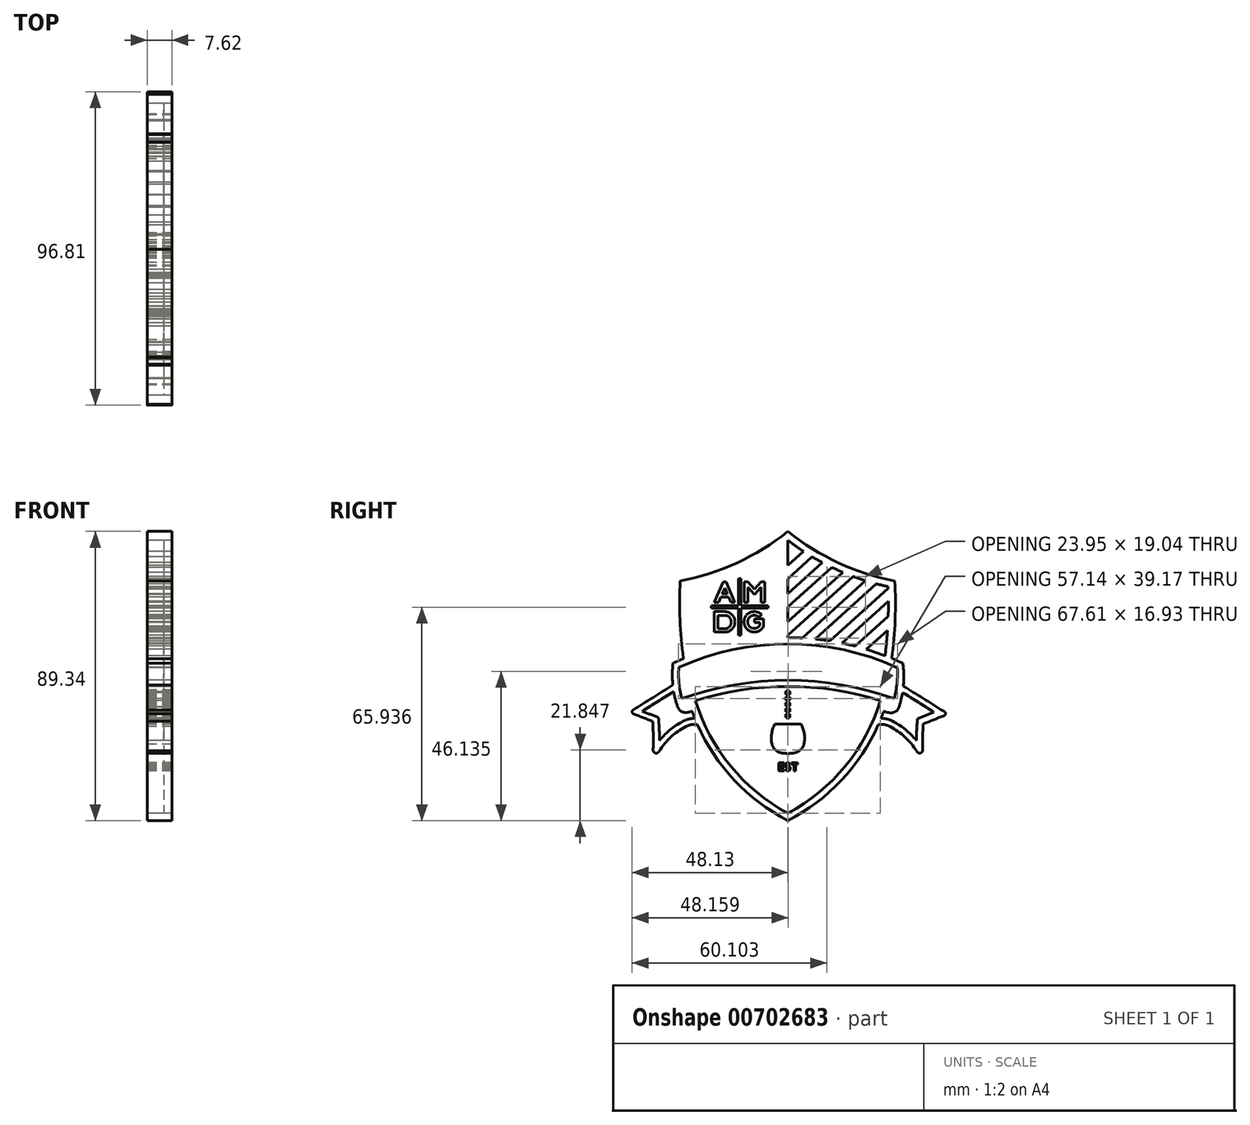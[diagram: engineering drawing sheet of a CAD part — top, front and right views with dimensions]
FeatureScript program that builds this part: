
annotation { "Feature Type Name" : "Feature", "Feature Type Description" : "" }
export const myFeature = defineFeature(function(context is Context, id is Id, definition is map)
    precondition{}
    {
        {
            var Q0;
            Q0=qCreatedBy(makeId("Right.planeOp"),FACE);
            var sketch = newSketch(context, id + "F0", { "sketchPlane" : qUnion([Q0])});
            skArc(sketch, "E0", {"start": v(-30.47, -7.29) * mm, "mid": v(-18.91, -28.58) * mm, "end": v(0, -43.73) * mm});
            skLineSegment(sketch, "E1", {"start": v(0, -43.73) * mm, "end": v(0, -41.47) * mm});
            skArc(sketch, "E2", {"start": v(0, -41.47) * mm, "mid": v(17.72, -26.9) * mm, "end": v(28.57, -6.67) * mm});
            skArc(sketch, "E3", {"start": v(0, -43.73) * mm, "mid": v(18.91, -28.58) * mm, "end": v(30.47, -7.29) * mm});
            skArc(sketch, "E4", {"start": v(-28.57, -6.67) * mm, "mid": v(-17.72, -26.9) * mm, "end": v(0, -41.47) * mm});
            skLineSegment(sketch, "E5", {"start": v(-14.58, 21.87) * mm, "end": v(-6.19, 21.87) * mm});
            skLineSegment(sketch, "E6", {"start": v(-6.19, 21.87) * mm, "end": v(-6.19, 22.63) * mm});
            skLineSegment(sketch, "E7", {"start": v(-6.19, 22.63) * mm, "end": v(-14.58, 22.63) * mm});
            skLineSegment(sketch, "E8", {"start": v(-14.58, 22.63) * mm, "end": v(-14.58, 31.02) * mm});
            skLineSegment(sketch, "E9", {"start": v(-14.58, 31.02) * mm, "end": v(-15.34, 31.02) * mm});
            skLineSegment(sketch, "E10", {"start": v(-15.34, 22.63) * mm, "end": v(-23.73, 22.63) * mm});
            skLineSegment(sketch, "E11", {"start": v(-23.73, 22.63) * mm, "end": v(-23.73, 21.87) * mm});
            skLineSegment(sketch, "E12", {"start": v(-15.34, 21.87) * mm, "end": v(-15.34, 13.48) * mm});
            skLineSegment(sketch, "E13", {"start": v(-15.34, 13.48) * mm, "end": v(-14.58, 13.48) * mm});
            skLineSegment(sketch, "E14", {"start": v(-14.58, 13.48) * mm, "end": v(-14.58, 21.87) * mm});
            skLineSegment(sketch, "E15", {"start": v(-19.04, 30) * mm, "end": v(-20.03, 30) * mm});
            skLineSegment(sketch, "E16", {"start": v(-20.03, 30) * mm, "end": v(-22.71, 23.64) * mm});
            skLineSegment(sketch, "E17", {"start": v(-15.34, 31.02) * mm, "end": v(-15.34, 22.63) * mm});
            skLineSegment(sketch, "E18", {"start": v(-16.35, 23.64) * mm, "end": v(-17.62, 23.64) * mm});
            skLineSegment(sketch, "E19", {"start": v(-22.71, 23.64) * mm, "end": v(-21.43, 23.64) * mm});
            skLineSegment(sketch, "E20", {"start": v(-20.3, 26.31) * mm, "end": v(-18.75, 26.31) * mm});
            skLineSegment(sketch, "E21", {"start": v(-18.75, 26.31) * mm, "end": v(-19.53, 28.16) * mm});
            skLineSegment(sketch, "E22", {"start": v(-20.3, 26.31) * mm, "end": v(-19.53, 28.16) * mm});
            skLineSegment(sketch, "E23", {"start": v(-20.74, 25.3) * mm, "end": v(-21.43, 23.64) * mm});
            skLineSegment(sketch, "E24", {"start": v(-20.74, 25.3) * mm, "end": v(-18.32, 25.3) * mm});
            skLineSegment(sketch, "E25", {"start": v(-18.32, 25.3) * mm, "end": v(-17.62, 23.64) * mm});
            skLineSegment(sketch, "E26", {"start": v(-12.42, 23.64) * mm, "end": v(-12.42, 28.45) * mm});
            skLineSegment(sketch, "E27", {"start": v(-7.2, 23.64) * mm, "end": v(-8.36, 23.64) * mm});
            skLineSegment(sketch, "E28", {"start": v(-8.36, 23.64) * mm, "end": v(-8.36, 28.45) * mm});
            skLineSegment(sketch, "E29", {"start": v(-12.42, 28.45) * mm, "end": v(-10.39, 26.16) * mm});
            skLineSegment(sketch, "E30", {"start": v(-10.39, 26.16) * mm, "end": v(-8.36, 28.45) * mm});
            skLineSegment(sketch, "E31", {"start": v(-7.2, 30) * mm, "end": v(-7.2, 23.64) * mm});
            skLineSegment(sketch, "E32", {"start": v(-12.42, 23.64) * mm, "end": v(-13.56, 23.64) * mm});
            skLineSegment(sketch, "E33", {"start": v(-13.56, 30) * mm, "end": v(-13.56, 23.64) * mm});
            skLineSegment(sketch, "E34", {"start": v(-19.04, 30) * mm, "end": v(-16.35, 23.64) * mm});
            skLineSegment(sketch, "E35", {"start": v(-7.2, 30) * mm, "end": v(-8.36, 30) * mm});
            skLineSegment(sketch, "E36", {"start": v(-8.36, 30) * mm, "end": v(-10.39, 27.79) * mm});
            skLineSegment(sketch, "E37", {"start": v(-13.56, 30) * mm, "end": v(-12.42, 30) * mm});
            skLineSegment(sketch, "E38", {"start": v(-12.42, 30) * mm, "end": v(-10.39, 27.79) * mm});
            skLineSegment(sketch, "E39", {"start": v(-22.71, 20.84) * mm, "end": v(-22.71, 14.5) * mm});
            skLineSegment(sketch, "E40", {"start": v(-21.58, 15.52) * mm, "end": v(-21.58, 19.69) * mm});
            skLineSegment(sketch, "E41", {"start": v(-23.73, 21.87) * mm, "end": v(-15.34, 21.87) * mm});
            skLineSegment(sketch, "E42", {"start": v(-8.96, 19.12) * mm, "end": v(-8.15, 19.93) * mm});
            skLineSegment(sketch, "E43", {"start": v(-10.3, 18.56) * mm, "end": v(-7.6, 18.56) * mm});
            skLineSegment(sketch, "E44", {"start": v(-10.3, 18.56) * mm, "end": v(-10.3, 17.42) * mm});
            skLineSegment(sketch, "E45", {"start": v(-10.3, 17.42) * mm, "end": v(-8.73, 17.42) * mm});
            skArc(sketch, "E46", {"start": v(34.3, -8.67) * mm, "mid": v(0.13, -2.3) * mm, "end": v(-34.07, -8.58) * mm});
            skArc(sketch, "E47", {"start": v(34.3, -8.67) * mm, "mid": v(35.68, -1.97) * mm, "end": v(35.5, 4.87) * mm});
            skArc(sketch, "E48", {"start": v(-35.5, 4.87) * mm, "mid": v(-35.55, -1.94) * mm, "end": v(-34.07, -8.58) * mm});
            skArc(sketch, "E49", {"start": v(31.82, -12.76) * mm, "mid": v(30.32, -12.3) * mm, "end": v(28.76, -12.14) * mm});
            skArc(sketch, "E50", {"start": v(39.69, -19) * mm, "mid": v(36.1, -15.44) * mm, "end": v(31.82, -12.76) * mm});
            skArc(sketch, "E51", {"start": v(40.04, -12.2) * mm, "mid": v(39.79, -15.6) * mm, "end": v(39.69, -19) * mm});
            skArc(sketch, "E52", {"start": v(40.04, -12.2) * mm, "mid": v(42.57, -11.26) * mm, "end": v(45.08, -10.26) * mm});
            skArc(sketch, "E53", {"start": v(45.08, -10.26) * mm, "mid": v(40.29, -7.15) * mm, "end": v(35.4, -4.2) * mm});
            skArc(sketch, "E54", {"start": v(41.83, -13.82) * mm, "mid": v(41.63, -17.96) * mm, "end": v(41.66, -22.11) * mm});
            skArc(sketch, "E55", {"start": v(47.88, -11.44) * mm, "mid": v(48.68, -10.69) * mm, "end": v(47.93, -9.9) * mm});
            skArc(sketch, "E56", {"start": v(41.83, -13.82) * mm, "mid": v(44.86, -12.64) * mm, "end": v(47.88, -11.44) * mm});
            skArc(sketch, "E57", {"start": v(47.93, -9.9) * mm, "mid": v(41.81, -6) * mm, "end": v(35.66, -2.16) * mm});
            skArc(sketch, "E58", {"start": v(31.55, -14.68) * mm, "mid": v(29.8, -14.07) * mm, "end": v(27.95, -14.05) * mm});
            skArc(sketch, "E59", {"start": v(39.78, -22.32) * mm, "mid": v(40.8, -22.88) * mm, "end": v(41.66, -22.11) * mm});
            skArc(sketch, "E60", {"start": v(39.78, -22.32) * mm, "mid": v(36.2, -17.94) * mm, "end": v(31.55, -14.68) * mm});
            skArc(sketch, "E61", {"start": v(-40, -11.94) * mm, "mid": v(-42.5, -10.91) * mm, "end": v(-45.03, -9.99) * mm});
            skArc(sketch, "E62", {"start": v(-31.82, -12.76) * mm, "mid": v(-36.1, -15.44) * mm, "end": v(-39.69, -19) * mm});
            skArc(sketch, "E63", {"start": v(-39.69, -19) * mm, "mid": v(-39.76, -15.47) * mm, "end": v(-40, -11.94) * mm});
            skArc(sketch, "E64", {"start": v(-35.27, -3.92) * mm, "mid": v(-40.2, -6.87) * mm, "end": v(-45.03, -9.99) * mm});
            skArc(sketch, "E65", {"start": v(-28.76, -12.14) * mm, "mid": v(-30.32, -12.3) * mm, "end": v(-31.82, -12.76) * mm});
            skArc(sketch, "E66", {"start": v(-35.55, -1.89) * mm, "mid": v(-41.74, -5.73) * mm, "end": v(-47.89, -9.62) * mm});
            skArc(sketch, "E67", {"start": v(-47.85, -10.66) * mm, "mid": v(-44.83, -11.86) * mm, "end": v(-41.8, -13.04) * mm});
            skArc(sketch, "E68", {"start": v(-41.66, -22.11) * mm, "mid": v(-41.59, -17.57) * mm, "end": v(-41.8, -13.04) * mm});
            skArc(sketch, "E69", {"start": v(-31.55, -14.68) * mm, "mid": v(-36.2, -17.94) * mm, "end": v(-39.78, -22.32) * mm});
            skArc(sketch, "E70", {"start": v(-41.66, -22.11) * mm, "mid": v(-40.8, -22.88) * mm, "end": v(-39.78, -22.32) * mm});
            skArc(sketch, "E71", {"start": v(-27.95, -14.05) * mm, "mid": v(-29.8, -14.07) * mm, "end": v(-31.55, -14.68) * mm});
            skArc(sketch, "E72", {"start": v(-47.89, -9.62) * mm, "mid": v(-48.13, -10.15) * mm, "end": v(-47.85, -10.66) * mm});
            skArc(sketch, "E73", {"start": v(-33.7, 3.57) * mm, "mid": v(-33.65, -1.27) * mm, "end": v(-32.82, -6.05) * mm});
            skArc(sketch, "E74", {"start": v(32.85, -6.06) * mm, "mid": v(33.69, -1.3) * mm, "end": v(33.8, 3.53) * mm});
            skArc(sketch, "E75", {"start": v(31.94, -10.43) * mm, "mid": v(33.41, -9.94) * mm, "end": v(34.3, -8.67) * mm});
            skArc(sketch, "E76", {"start": v(-34.07, -8.58) * mm, "mid": v(-33.17, -9.85) * mm, "end": v(-31.7, -10.34) * mm});
            skArc(sketch, "E77", {"start": v(29.6, -9.9) * mm, "mid": v(30.74, -10.3) * mm, "end": v(31.94, -10.43) * mm});
            skArc(sketch, "E78", {"start": v(-31.7, -10.34) * mm, "mid": v(-30.63, -10.23) * mm, "end": v(-29.6, -9.9) * mm});
            skLineSegment(sketch, "E79", {"start": v(-7.6, 18.56) * mm, "end": v(-7.6, 16.28) * mm});
            skLineSegment(sketch, "E80", {"start": v(-8.73, 17.42) * mm, "end": v(-8.73, 16.6) * mm});
            skArc(sketch, "E81", {"start": v(-7.64, 16.08) * mm, "mid": v(-7.6, 16.18) * mm, "end": v(-7.6, 16.28) * mm});
            skArc(sketch, "E82", {"start": v(-8.82, 16.38) * mm, "mid": v(-8.75, 16.48) * mm, "end": v(-8.73, 16.6) * mm});
            skArc(sketch, "E83", {"start": v(-8.96, 19.12) * mm, "mid": v(-12.43, 17.57) * mm, "end": v(-8.82, 16.38) * mm});
            skArc(sketch, "E84", {"start": v(-8.15, 19.93) * mm, "mid": v(-13.54, 17.26) * mm, "end": v(-7.64, 16.08) * mm});
            skLineSegment(sketch, "E85", {"start": v(-22.71, 20.84) * mm, "end": v(-19.55, 20.84) * mm});
            skLineSegment(sketch, "E86", {"start": v(-22.71, 14.5) * mm, "end": v(-19.55, 14.5) * mm});
            skArc(sketch, "E87", {"start": v(-19.55, 14.5) * mm, "mid": v(-16.35, 17.67) * mm, "end": v(-19.55, 20.84) * mm});
            skLineSegment(sketch, "E88", {"start": v(-21.58, 15.52) * mm, "end": v(-19.55, 15.52) * mm});
            skLineSegment(sketch, "E89", {"start": v(-21.58, 19.69) * mm, "end": v(-19.55, 19.69) * mm});
            skArc(sketch, "E90", {"start": v(-19.55, 15.52) * mm, "mid": v(-17.5, 17.6) * mm, "end": v(-19.55, 19.69) * mm});
            skArc(sketch, "E91", {"start": v(35.5, 4.87) * mm, "mid": v(0, 12.8) * mm, "end": v(-35.5, 4.87) * mm});
            skLineSegment(sketch, "E92", {"start": v(0, 12.8) * mm, "end": v(0, 10.87) * mm});
            skArc(sketch, "E93", {"start": v(32.09, 6.38) * mm, "mid": v(33.12, 18.33) * mm, "end": v(33.02, 30.33) * mm});
            skArc(sketch, "E94", {"start": v(30, 7.22) * mm, "mid": v(30.93, 17.87) * mm, "end": v(30.93, 28.56) * mm});
            skLineSegment(sketch, "E95", {"start": v(0, 42.88) * mm, "end": v(0, 12.8) * mm});
            skArc(sketch, "E96", {"start": v(-30.92, 28.57) * mm, "mid": v(-30.9, 18) * mm, "end": v(-29.98, 7.47) * mm});
            skArc(sketch, "E97", {"start": v(-33.27, 30.28) * mm, "mid": v(-33.34, 18.27) * mm, "end": v(-32.27, 6.3) * mm});
            skArc(sketch, "E98", {"start": v(-30.92, 28.57) * mm, "mid": v(-14.68, 34.03) * mm, "end": v(0, 42.88) * mm});
            skArc(sketch, "E99", {"start": v(0, 42.88) * mm, "mid": v(14.66, 34) * mm, "end": v(30.93, 28.56) * mm});
            skArc(sketch, "E100", {"start": v(0, 45.61) * mm, "mid": v(15.57, 35.94) * mm, "end": v(33.02, 30.33) * mm});
            skArc(sketch, "E101", {"start": v(-33.27, 30.28) * mm, "mid": v(-15.7, 35.93) * mm, "end": v(0, 45.61) * mm});
            skLineSegment(sketch, "E102", {"start": v(4.8, 39.47) * mm, "end": v(0, 35.12) * mm});
            skLineSegment(sketch, "E103", {"start": v(7.5, 37.77) * mm, "end": v(0, 30.99) * mm});
            skLineSegment(sketch, "E104", {"start": v(10.62, 36.01) * mm, "end": v(0, 26.4) * mm});
            skLineSegment(sketch, "E105", {"start": v(13.55, 34.52) * mm, "end": v(0, 22.27) * mm});
            skLineSegment(sketch, "E106", {"start": v(16.92, 33) * mm, "end": v(0, 17.69) * mm});
            skLineSegment(sketch, "E107", {"start": v(20.1, 31.73) * mm, "end": v(0, 13.55) * mm});
            skLineSegment(sketch, "E108", {"start": v(23.95, 30.4) * mm, "end": v(4.36, 12.69) * mm});
            skLineSegment(sketch, "E109", {"start": v(27.27, 29.44) * mm, "end": v(8.4, 12.38) * mm});
            skLineSegment(sketch, "E110", {"start": v(12.97, 11.79) * mm, "end": v(30.95, 28.05) * mm});
            skLineSegment(sketch, "E111", {"start": v(31.04, 24.03) * mm, "end": v(16.75, 11.1) * mm});
            skLineSegment(sketch, "E112", {"start": v(30.98, 19.34) * mm, "end": v(20.77, 10.17) * mm});
            skLineSegment(sketch, "E113", {"start": v(24.27, 9.2) * mm, "end": v(30.77, 15.07) * mm});
            skArc(sketch, "E114", {"start": v(33.8, 3.53) * mm, "mid": v(0.05, 10.87) * mm, "end": v(-33.7, 3.57) * mm});
            skArc(sketch, "E115", {"start": v(32.85, -6.06) * mm, "mid": v(0.02, -0.36) * mm, "end": v(-32.82, -6.05) * mm});
            skSolve(sketch);
        }
        {
            var Q0;
            Q0=qCreatedBy(makeId("Right.planeOp"),FACE);
            var sketch = newSketch(context, id + "F1", { "sketchPlane" : qUnion([Q0])});
            skLineSegment(sketch, "E116", {"start": v(0, -3.35) * mm, "end": v(0.9, -4.25) * mm});
            skLineSegment(sketch, "E117", {"start": v(-0.9, -4.25) * mm, "end": v(0, -3.35) * mm});
            skLineSegment(sketch, "E118", {"start": v(-0.9, -4.25) * mm, "end": v(0, -5.14) * mm});
            skLineSegment(sketch, "E119", {"start": v(0, -5.14) * mm, "end": v(0.9, -4.25) * mm});
            skLineSegment(sketch, "E120", {"start": v(0, -5.14) * mm, "end": v(-0.9, -6.03) * mm});
            skLineSegment(sketch, "E121", {"start": v(-0.9, -6.03) * mm, "end": v(0, -6.92) * mm});
            skLineSegment(sketch, "E122", {"start": v(0, -5.14) * mm, "end": v(0.9, -6.03) * mm});
            skLineSegment(sketch, "E123", {"start": v(0.9, -6.03) * mm, "end": v(0, -6.92) * mm});
            skLineSegment(sketch, "E124", {"start": v(0, -6.92) * mm, "end": v(-0.9, -7.82) * mm});
            skLineSegment(sketch, "E125", {"start": v(0, -6.92) * mm, "end": v(0.9, -7.82) * mm});
            skLineSegment(sketch, "E126", {"start": v(0.9, -7.82) * mm, "end": v(0, -8.71) * mm});
            skLineSegment(sketch, "E127", {"start": v(0, -8.71) * mm, "end": v(-0.9, -7.82) * mm});
            skLineSegment(sketch, "E128", {"start": v(0, -8.71) * mm, "end": v(0.9, -9.6) * mm});
            skLineSegment(sketch, "E129", {"start": v(0, -8.71) * mm, "end": v(-0.9, -9.6) * mm});
            skLineSegment(sketch, "E130", {"start": v(-0.9, -9.6) * mm, "end": v(0, -10.5) * mm});
            skLineSegment(sketch, "E131", {"start": v(0.9, -9.6) * mm, "end": v(0, -10.5) * mm});
            skLineSegment(sketch, "E132", {"start": v(0.9, -11.39) * mm, "end": v(0, -10.5) * mm});
            skLineSegment(sketch, "E133", {"start": v(-0.9, -11.39) * mm, "end": v(0, -12.28) * mm});
            skLineSegment(sketch, "E134", {"start": v(0.9, -11.39) * mm, "end": v(0, -12.28) * mm});
            skLineSegment(sketch, "E135", {"start": v(-0.9, -11.39) * mm, "end": v(0, -10.5) * mm});
            skLineSegment(sketch, "E136", {"start": v(0, -10.96) * mm, "end": v(-0.45, -11.4) * mm});
            skLineSegment(sketch, "E137", {"start": v(0, -10.96) * mm, "end": v(0.45, -11.4) * mm});
            skLineSegment(sketch, "E138", {"start": v(0.45, -11.4) * mm, "end": v(0, -11.86) * mm});
            skLineSegment(sketch, "E139", {"start": v(0, -11.86) * mm, "end": v(-0.45, -11.4) * mm});
            skLineSegment(sketch, "E140", {"start": v(0, -10.07) * mm, "end": v(0.45, -9.62) * mm});
            skLineSegment(sketch, "E141", {"start": v(0.45, -9.62) * mm, "end": v(0, -9.17) * mm});
            skLineSegment(sketch, "E142", {"start": v(0, -9.17) * mm, "end": v(-0.45, -9.62) * mm});
            skLineSegment(sketch, "E143", {"start": v(-0.45, -9.62) * mm, "end": v(0, -10.07) * mm});
            skLineSegment(sketch, "E144", {"start": v(0, -7.38) * mm, "end": v(-0.45, -7.83) * mm});
            skLineSegment(sketch, "E145", {"start": v(-0.45, -7.83) * mm, "end": v(0, -8.28) * mm});
            skLineSegment(sketch, "E146", {"start": v(0, -8.28) * mm, "end": v(0.45, -7.83) * mm});
            skLineSegment(sketch, "E147", {"start": v(0.45, -7.83) * mm, "end": v(0, -7.38) * mm});
            skLineSegment(sketch, "E148", {"start": v(0, -6.49) * mm, "end": v(0.45, -6.04) * mm});
            skLineSegment(sketch, "E149", {"start": v(0.45, -6.04) * mm, "end": v(0, -5.6) * mm});
            skLineSegment(sketch, "E150", {"start": v(0, -5.6) * mm, "end": v(-0.45, -6.04) * mm});
            skLineSegment(sketch, "E151", {"start": v(-0.45, -6.04) * mm, "end": v(0, -6.49) * mm});
            skLineSegment(sketch, "E152", {"start": v(0, -3.8) * mm, "end": v(0.45, -4.24) * mm});
            skLineSegment(sketch, "E153", {"start": v(0.45, -4.24) * mm, "end": v(0, -4.69) * mm});
            skLineSegment(sketch, "E154", {"start": v(-0.45, -4.24) * mm, "end": v(0, -4.69) * mm});
            skLineSegment(sketch, "E155", {"start": v(-0.45, -4.24) * mm, "end": v(0, -3.8) * mm});
            skLineSegment(sketch, "E156", {"start": v(0, -30) * mm, "end": v(0, -34.18) * mm});
            skLineSegment(sketch, "E157", {"start": v(0, -34.18) * mm, "end": v(5.89, -34.18) * mm});
            skLineSegment(sketch, "E158", {"start": v(5.89, -34.18) * mm, "end": v(5.89, -30) * mm});
            skLineSegment(sketch, "E159", {"start": v(5.89, -30) * mm, "end": v(0, -30) * mm});
            skLineSegment(sketch, "E160", {"start": v(0, -30) * mm, "end": v(-5.89, -30) * mm});
            skLineSegment(sketch, "E161", {"start": v(-5.89, -30) * mm, "end": v(-5.89, -34.18) * mm});
            skLineSegment(sketch, "E162", {"start": v(-5.89, -34.18) * mm, "end": v(0, -34.18) * mm});
            skLineSegment(sketch, "E163", {"start": v(-0.25, -27.7) * mm, "end": v(-0.73, -27.88) * mm});
            skLineSegment(sketch, "E164", {"start": v(0.23, -26.47) * mm, "end": v(0.7, -26.28) * mm});
            skLineSegment(sketch, "E165", {"start": v(1.13, -26.3) * mm, "end": v(1.13, -25.8) * mm});
            skLineSegment(sketch, "E166", {"start": v(1.13, -25.8) * mm, "end": v(3.03, -25.8) * mm});
            skLineSegment(sketch, "E167", {"start": v(3.03, -25.8) * mm, "end": v(3.03, -26.3) * mm});
            skLineSegment(sketch, "E168", {"start": v(2.33, -26.3) * mm, "end": v(3.03, -26.3) * mm});
            skLineSegment(sketch, "E169", {"start": v(1.83, -26.3) * mm, "end": v(1.13, -26.3) * mm});
            skLineSegment(sketch, "E170", {"start": v(1.83, -26.3) * mm, "end": v(1.83, -28.34) * mm});
            skLineSegment(sketch, "E171", {"start": v(1.83, -28.34) * mm, "end": v(2.33, -28.34) * mm});
            skLineSegment(sketch, "E172", {"start": v(2.33, -28.34) * mm, "end": v(2.33, -26.3) * mm});
            skLineSegment(sketch, "E173", {"start": v(-1.14, -26.3) * mm, "end": v(-1.14, -25.8) * mm});
            skLineSegment(sketch, "E174", {"start": v(-1.14, -28.34) * mm, "end": v(-1.14, -27.83) * mm});
            skLineSegment(sketch, "E175", {"start": v(-2.3, -26.3) * mm, "end": v(-2.3, -26.8) * mm});
            skLineSegment(sketch, "E176", {"start": v(-2.3, -27.31) * mm, "end": v(-2.3, -27.83) * mm});
            skLineSegment(sketch, "E177", {"start": v(-2.8, -25.8) * mm, "end": v(-2.8, -28.34) * mm});
            skLineSegment(sketch, "E178", {"start": v(-2.8, -25.8) * mm, "end": v(-1.14, -25.8) * mm});
            skLineSegment(sketch, "E179", {"start": v(-1.14, -28.34) * mm, "end": v(-2.8, -28.34) * mm});
            skLineSegment(sketch, "E180", {"start": v(-2.3, -26.3) * mm, "end": v(-1.14, -26.3) * mm});
            skLineSegment(sketch, "E181", {"start": v(-2.3, -27.83) * mm, "end": v(-1.14, -27.83) * mm});
            skLineSegment(sketch, "E182", {"start": v(-1.27, -26.8) * mm, "end": v(-1.27, -27.31) * mm});
            skLineSegment(sketch, "E183", {"start": v(-1.27, -27.31) * mm, "end": v(-2.3, -27.31) * mm});
            skLineSegment(sketch, "E184", {"start": v(-2.3, -26.8) * mm, "end": v(-1.27, -26.8) * mm});
            skLineSegment(sketch, "E185", {"start": v(0, -13.91) * mm, "end": v(4.06, -13.91) * mm});
            skLineSegment(sketch, "E186", {"start": v(0, -13.91) * mm, "end": v(-4.06, -13.91) * mm});
            skArc(sketch, "E187", {"start": v(4.95, -20.14) * mm, "mid": v(5.06, -16.95) * mm, "end": v(4.06, -13.91) * mm});
            skArc(sketch, "E188", {"start": v(1.92, -22.83) * mm, "mid": v(3.82, -21.91) * mm, "end": v(4.95, -20.14) * mm});
            skArc(sketch, "E189", {"start": v(-4.93, -20.14) * mm, "mid": v(-3.8, -21.91) * mm, "end": v(-1.9, -22.83) * mm});
            skArc(sketch, "E190", {"start": v(-4.06, -13.91) * mm, "mid": v(-5.04, -16.95) * mm, "end": v(-4.93, -20.14) * mm});
            skArc(sketch, "E191", {"start": v(-1.9, -22.83) * mm, "mid": v(0, -23) * mm, "end": v(1.92, -22.83) * mm});
            skArc(sketch, "E192", {"start": v(-0.73, -27.88) * mm, "mid": v(0.63, -28.03) * mm, "end": v(0, -26.83) * mm});
            skArc(sketch, "E193", {"start": v(-0.25, -27.7) * mm, "mid": v(0.2, -27.74) * mm, "end": v(0, -27.34) * mm});
            skArc(sketch, "E194", {"start": v(0.7, -26.28) * mm, "mid": v(-0.65, -26.14) * mm, "end": v(0, -27.34) * mm});
            skArc(sketch, "E195", {"start": v(0.23, -26.47) * mm, "mid": v(-0.22, -26.43) * mm, "end": v(0, -26.83) * mm});
            skSolve(sketch);
        }
        {
            var Q0;
            {var subQ3=sQuery(id+"F0.wireOp",EDGE,"ONLfzzXL-3R4D-800U-wvTq-QPhKhhyo4mzz");Q0=makeQuery(id+"F0.imprint","IMPRINT",FACE,{"disambiguationData":[TD([[makeQuery(id+"F0.imprint","IMPRINT",EDGE,{"derivedFrom":subQ3}),1.0]])]});}
            var Q1;
            {var subQ3=sQuery(id+"F0.wireOp",EDGE,"E1");Q1=makeQuery(id+"F0.imprint","IMPRINT",FACE,{"disambiguationData":[TD([[makeQuery(id+"F0.imprint","IMPRINT",EDGE,{"derivedFrom":subQ3}),-1.0]])]});}
            var Q2;
            {var subQ1=sQuery(id+"F0.wireOp",EDGE,"BdnYPgPC-IgTI-QKEn-dc1g-fA2m82bS0SO2");Q2=makeQuery(id+"F0.imprint","IMPRINT",FACE,{"disambiguationData":[TD([[makeQuery(id+"F0.imprint","IMPRINT",EDGE,{"derivedFrom":subQ1}),1.0]])]});}
            var Q3;
            {var subQ8=sQuery(id+"F0.wireOp",EDGE,"ONLfzzXL-3R4D-800U-wvTq-QPhKhhyo4mzz");Q3=makeQuery(id+"F0.imprint","IMPRINT",FACE,{"disambiguationData":[TD([[makeQuery(id+"F0.imprint","IMPRINT",EDGE,{"derivedFrom":subQ8}),-1.0]])]});}
            var Q4;
            {var subQ23=sQuery(id+"F0.wireOp",EDGE,"8WM0Bcwe-3rc9-BwEm-lvAE-P2pIR12rDpk2");Q4=makeQuery(id+"F0.imprint","IMPRINT",FACE,{"disambiguationData":[TD([[makeQuery(id+"F0.imprint","IMPRINT",EDGE,{"derivedFrom":subQ23}),1.0]])]});}
            var Q5;
            {var subQ0=sQuery(id+"F0.wireOp",EDGE,"bnOI33SO-Lt5R-RXRq-jggM-VqTzbiWvbtrV");Q5=makeQuery(id+"F0.imprint","IMPRINT",FACE,{"disambiguationData":[TD([[makeQuery(id+"F0.imprint","IMPRINT",EDGE,{"derivedFrom":subQ0}),-1.0]])]});}
            var Q6;
            {var subQ0=sQuery(id+"F0.wireOp",EDGE,"4LBZazxE-MXz6-BxoV-xFqA-rfLyMIYtJeZZ");Q6=makeQuery(id+"F0.imprint","IMPRINT",FACE,{"disambiguationData":[TD([[makeQuery(id+"F0.imprint","IMPRINT",EDGE,{"derivedFrom":subQ0}),-1.0]])]});}
            var Q7;
            {var subQ0=sQuery(id+"F0.wireOp",EDGE,"RIueIUBm-ODRK-q0LA-V08c-46jnks9BpBTh");Q7=makeQuery(id+"F0.imprint","IMPRINT",FACE,{"disambiguationData":[TD([[makeQuery(id+"F0.imprint","IMPRINT",EDGE,{"derivedFrom":subQ0}),1.0]])]});}
            var Q8;
            Q8=makeQuery(id+"F0.imprint","IMPRINT",FACE,{"disambiguationData":[TD([[makeQuery(id+"F0.imprint","IMPRINT",EDGE,{"derivedFrom":sQuery(id+"F0.wireOp",EDGE,"E20")}),1.0]])]});
            var Q9;
            Q9=makeQuery(id+"F0.imprint","IMPRINT",FACE,{"disambiguationData":[TD([[makeQuery(id+"F0.imprint","IMPRINT",EDGE,{"derivedFrom":sQuery(id+"F0.wireOp",EDGE,"E40")}),-1.0]])]});
            var Q10;
            {var subQ0=sQuery(id+"F0.wireOp",EDGE,"nFxFFDrl-6lil-AD3G-HWLL-AWG5huvdxhyb");Q10=makeQuery(id+"F0.imprint","IMPRINT",FACE,{"disambiguationData":[TD([[makeQuery(id+"F0.imprint","IMPRINT",EDGE,{"derivedFrom":subQ0}),1.0]])]});}
            var Q11;
            {var subQ0=sQuery(id+"F0.wireOp",EDGE,"UkIwrnuq-Skmx-TIPs-jBmS-mAVkkgQC0Rbf");Q11=makeQuery(id+"F0.imprint","IMPRINT",FACE,{"disambiguationData":[TD([[makeQuery(id+"F0.imprint","IMPRINT",EDGE,{"derivedFrom":subQ0}),1.0]])]});}
            var Q12;
            {var subQ0=sQuery(id+"F0.wireOp",EDGE,"tndkFHdb-0dpU-zl5A-KN4j-1cjWgC935387");Q12=makeQuery(id+"F0.imprint","IMPRINT",FACE,{"disambiguationData":[TD([[makeQuery(id+"F0.imprint","IMPRINT",EDGE,{"derivedFrom":subQ0}),1.0]])]});}
            var Q13;
            {var subQ0=sQuery(id+"F0.wireOp",EDGE,"bmTnI2Um-67v4-zXO9-JvZs-pzyo4UbaBzVl");Q13=makeQuery(id+"F0.imprint","IMPRINT",FACE,{"disambiguationData":[TD([[makeQuery(id+"F0.imprint","IMPRINT",EDGE,{"derivedFrom":subQ0}),1.0]])]});}
            var Q14;
            {var subQ0=sQuery(id+"F0.wireOp",EDGE,"E46");var subQ1=sQuery(id+"F0.wireOp",EDGE,"E0");var subQ2=makeQuery(id+"F0.imprint","INTERSECT",VERTEX,{"derivedFrom":[subQ1,subQ0]});Q14=makeQuery(id+"F0.imprint","IMPRINT",FACE,{"disambiguationData":[TD([[makeQuery(id+"F0.imprint","IMPRINT",EDGE,{"disambiguationData":[TD([[subQ2,-1.0]])],"derivedFrom":subQ1}),-1.0]])]});}
            var Q15;
            {var subQ0=sQuery(id+"F0.wireOp",EDGE,"E46");var subQ1=sQuery(id+"F0.wireOp",EDGE,"E2");var subQ2=makeQuery(id+"F0.imprint","INTERSECT",VERTEX,{"derivedFrom":[subQ1,subQ0]});Q15=makeQuery(id+"F0.imprint","IMPRINT",FACE,{"disambiguationData":[TD([[makeQuery(id+"F0.imprint","IMPRINT",EDGE,{"disambiguationData":[TD([[subQ2,1.0]])],"derivedFrom":subQ1}),-1.0]])]});}
            var Q16;
            {var subQ0=sQuery(id+"F0.wireOp",EDGE,"E46");var subQ1=sQuery(id+"F0.wireOp",EDGE,"E3");var subQ2=makeQuery(id+"F0.imprint","INTERSECT",VERTEX,{"derivedFrom":[subQ1,subQ0]});Q16=makeQuery(id+"F0.imprint","IMPRINT",FACE,{"disambiguationData":[TD([[makeQuery(id+"F0.imprint","IMPRINT",EDGE,{"disambiguationData":[TD([[subQ2,1.0]])],"derivedFrom":subQ1}),-1.0]])]});}
            var Q17;
            {var subQ0=sQuery(id+"F0.wireOp",EDGE,"ES58G5GB-QQ11-E4u9-2Vgj-w79NEhwHflgS");Q17=makeQuery(id+"F0.imprint","IMPRINT",FACE,{"disambiguationData":[TD([[makeQuery(id+"F0.imprint","IMPRINT",EDGE,{"derivedFrom":subQ0}),1.0]])]});}
            var Q18;
            {var subQ0=sQuery(id+"F0.wireOp",EDGE,"E49");Q18=makeQuery(id+"F0.imprint","IMPRINT",FACE,{"disambiguationData":[TD([[makeQuery(id+"F0.imprint","IMPRINT",EDGE,{"derivedFrom":subQ0}),1.0]])]});}
            var Q19;
            Q19=makeQuery(id+"F0.imprint","IMPRINT",FACE,{"disambiguationData":[TD([[makeQuery(id+"F0.imprint","IMPRINT",EDGE,{"derivedFrom":sQuery(id+"F0.wireOp",EDGE,"E61")}),1.0]])]});
            var Q20;
            {var subQ12=sQuery(id+"F0.wireOp",EDGE,"735V5g1R-ZVwF-Ptzb-ZYVV-kyU7RxEmZObx");Q20=makeQuery(id+"F0.imprint","IMPRINT",FACE,{"disambiguationData":[TD([[makeQuery(id+"F0.imprint","IMPRINT",EDGE,{"derivedFrom":subQ12}),1.0]])]});}
            var Q21;
            {var subQ17=sQuery(id+"F0.wireOp",EDGE,"735V5g1R-ZVwF-Ptzb-ZYVV-kyU7RxEmZObx");Q21=makeQuery(id+"F0.imprint","IMPRINT",FACE,{"disambiguationData":[TD([[makeQuery(id+"F0.imprint","IMPRINT",EDGE,{"derivedFrom":subQ17}),-1.0]])]});}
            var Q22;
            Q22=makeQuery(id+"F0.imprint","IMPRINT",FACE,{"disambiguationData":[TD([[makeQuery(id+"F0.imprint","IMPRINT",EDGE,{"derivedFrom":sQuery(id+"F0.wireOp",EDGE,"ZdOdTYM1-hNYq-ImzT-kX6W-GL3nDNaCb56i")}),1.0]])]});
            var Q23;
            {var subQ0=sQuery(id+"F0.wireOp",EDGE,"E1");Q23=makeQuery(id+"F0.imprint","IMPRINT",FACE,{"disambiguationData":[TD([[makeQuery(id+"F0.imprint","IMPRINT",EDGE,{"derivedFrom":subQ0}),1.0]])]});}
            var Q24;
            {var subQ5=sQuery(id+"F0.wireOp",EDGE,"E73");Q24=makeQuery(id+"F0.imprint","IMPRINT",FACE,{"disambiguationData":[TD([[makeQuery(id+"F0.imprint","IMPRINT",EDGE,{"derivedFrom":subQ5}),-1.0]])]});}
            var Q25;
            {var subQ4=sQuery(id+"F0.wireOp",EDGE,"E74");Q25=makeQuery(id+"F0.imprint","IMPRINT",FACE,{"disambiguationData":[TD([[makeQuery(id+"F0.imprint","IMPRINT",EDGE,{"derivedFrom":subQ4}),-1.0]])]});}
            var Q26;
            Q26=makeQuery(id+"F0.imprint","IMPRINT",FACE,{"disambiguationData":[TD([[makeQuery(id+"F0.imprint","IMPRINT",EDGE,{"derivedFrom":sQuery(id+"F0.wireOp",EDGE,"E5")}),-1.0]])]});
            var Q27;
            {var subQ0=sQuery(id+"F0.wireOp",EDGE,"E102");Q27=makeQuery(id+"F0.imprint","IMPRINT",FACE,{"disambiguationData":[TD([[makeQuery(id+"F0.imprint","IMPRINT",EDGE,{"derivedFrom":subQ0}),1.0]])]});}
            var Q28;
            {var subQ0=sQuery(id+"F0.wireOp",EDGE,"E104");Q28=makeQuery(id+"F0.imprint","IMPRINT",FACE,{"disambiguationData":[TD([[makeQuery(id+"F0.imprint","IMPRINT",EDGE,{"derivedFrom":subQ0}),1.0]])]});}
            var Q29;
            {var subQ0=sQuery(id+"F0.wireOp",EDGE,"E106");Q29=makeQuery(id+"F0.imprint","IMPRINT",FACE,{"disambiguationData":[TD([[makeQuery(id+"F0.imprint","IMPRINT",EDGE,{"derivedFrom":subQ0}),1.0]])]});}
            var Q30;
            {var subQ0=sQuery(id+"F0.wireOp",EDGE,"E108");Q30=makeQuery(id+"F0.imprint","IMPRINT",FACE,{"disambiguationData":[TD([[makeQuery(id+"F0.imprint","IMPRINT",EDGE,{"derivedFrom":subQ0}),1.0]])]});}
            var Q31;
            {var subQ0=sQuery(id+"F0.wireOp",EDGE,"E110");Q31=makeQuery(id+"F0.imprint","IMPRINT",FACE,{"disambiguationData":[TD([[makeQuery(id+"F0.imprint","IMPRINT",EDGE,{"derivedFrom":subQ0}),-1.0]])]});}
            var Q32;
            {var subQ0=sQuery(id+"F0.wireOp",EDGE,"E112");Q32=makeQuery(id+"F0.imprint","IMPRINT",FACE,{"disambiguationData":[TD([[makeQuery(id+"F0.imprint","IMPRINT",EDGE,{"derivedFrom":subQ0}),1.0]])]});}
            extrude(context, id + "F2", {"entities" : qUnion([Q0, Q1, Q2, Q3, Q4, Q5, Q6, Q7, Q8, Q9, Q10, Q11, Q12, Q13, Q14, Q15, Q16, Q17, Q18, Q19, Q20, Q21, Q22, Q23, Q24, Q25, Q26, Q27, Q28, Q29, Q30, Q31, Q32]), "depth" : 7.62 * mm, "offsetDistance" : 25.4 * mm});
        }
        {
            var Q0;
            {var subQ2=sQuery(id+"F0.wireOp",EDGE,"E73");Q0=makeQuery(id+"F0.imprint","IMPRINT",FACE,{"disambiguationData":[TD([[makeQuery(id+"F0.imprint","IMPRINT",EDGE,{"derivedFrom":subQ2}),1.0]])]});}
            var Q1;
            {var subQ1=sQuery(id+"F0.wireOp",EDGE,"bmTnI2Um-67v4-zXO9-JvZs-pzyo4UbaBzVl");Q1=makeQuery(id+"F0.imprint","IMPRINT",FACE,{"disambiguationData":[TD([[makeQuery(id+"F0.imprint","IMPRINT",EDGE,{"derivedFrom":subQ1}),-1.0]])]});}
            var Q2;
            {var subQ0=sQuery(id+"F0.wireOp",EDGE,"E2");Q2=makeQuery(id+"F0.imprint","IMPRINT",FACE,{"disambiguationData":[TD([[makeQuery(id+"F0.imprint","IMPRINT",EDGE,{"derivedFrom":subQ0}),1.0]])]});}
            var Q3;
            {var subQ4=sQuery(id+"F0.wireOp",EDGE,"ES58G5GB-QQ11-E4u9-2Vgj-w79NEhwHflgS");Q3=makeQuery(id+"F0.imprint","IMPRINT",FACE,{"disambiguationData":[TD([[makeQuery(id+"F0.imprint","IMPRINT",EDGE,{"derivedFrom":subQ4}),-1.0]])]});}
            var Q4;
            {var subQ3=sQuery(id+"F0.wireOp",EDGE,"DCwpawZ0-wABv-cR8x-EWj8-pZYnT6nsuBVQ");Q4=makeQuery(id+"F0.imprint","IMPRINT",FACE,{"disambiguationData":[TD([[makeQuery(id+"F0.imprint","IMPRINT",EDGE,{"derivedFrom":subQ3}),1.0]])]});}
            var Q5;
            {var subQ0=sQuery(id+"F0.wireOp",EDGE,"dIkKE2wf-rdH6-2kfd-aeEA-nJW8ELZktZna");Q5=makeQuery(id+"F0.imprint","IMPRINT",FACE,{"disambiguationData":[TD([[makeQuery(id+"F0.imprint","IMPRINT",EDGE,{"derivedFrom":subQ0}),1.0]])]});}
            var Q6;
            {var subQ0=sQuery(id+"F0.wireOp",EDGE,"ZzwVhsn8-AHJ3-veAE-n7mC-tu67IKEQpqe1");Q6=makeQuery(id+"F0.imprint","IMPRINT",FACE,{"disambiguationData":[TD([[makeQuery(id+"F0.imprint","IMPRINT",EDGE,{"derivedFrom":subQ0}),1.0]])]});}
            var Q7;
            {var subQ2=sQuery(id+"F0.wireOp",EDGE,"RIueIUBm-ODRK-q0LA-V08c-46jnks9BpBTh");Q7=makeQuery(id+"F0.imprint","IMPRINT",FACE,{"disambiguationData":[TD([[makeQuery(id+"F0.imprint","IMPRINT",EDGE,{"derivedFrom":subQ2}),-1.0]])]});}
            var Q8;
            {var subQ0=sQuery(id+"F0.wireOp",EDGE,"PXlrvZXc-IWCi-jHwB-2z6x-I1Kd2UGDQcSo");Q8=makeQuery(id+"F0.imprint","IMPRINT",FACE,{"disambiguationData":[TD([[makeQuery(id+"F0.imprint","IMPRINT",EDGE,{"derivedFrom":subQ0}),-1.0]])]});}
            var Q9;
            {var subQ0=sQuery(id+"F0.wireOp",EDGE,"4Uymkrsu-ucGw-Rutd-ytz0-wluclODmey34");Q9=makeQuery(id+"F0.imprint","IMPRINT",FACE,{"disambiguationData":[TD([[makeQuery(id+"F0.imprint","IMPRINT",EDGE,{"derivedFrom":subQ0}),-1.0]])]});}
            var Q10;
            {var subQ0=sQuery(id+"F0.wireOp",EDGE,"bnOI33SO-Lt5R-RXRq-jggM-VqTzbiWvbtrV");Q10=makeQuery(id+"F0.imprint","IMPRINT",FACE,{"disambiguationData":[TD([[makeQuery(id+"F0.imprint","IMPRINT",EDGE,{"derivedFrom":subQ0}),1.0]])]});}
            var Q11;
            Q11=makeQuery(id+"F0.imprint","IMPRINT",FACE,{"disambiguationData":[TD([[makeQuery(id+"F0.imprint","IMPRINT",EDGE,{"derivedFrom":sQuery(id+"F0.wireOp",EDGE,"E26")}),1.0]])]});
            var Q12;
            Q12=makeQuery(id+"F0.imprint","IMPRINT",FACE,{"disambiguationData":[TD([[makeQuery(id+"F0.imprint","IMPRINT",EDGE,{"derivedFrom":sQuery(id+"F0.wireOp",EDGE,"E15")}),1.0]])]});
            var Q13;
            Q13=makeQuery(id+"F0.imprint","IMPRINT",FACE,{"disambiguationData":[TD([[makeQuery(id+"F0.imprint","IMPRINT",EDGE,{"derivedFrom":sQuery(id+"F0.wireOp",EDGE,"E39")}),1.0]])]});
            var Q14;
            Q14=makeQuery(id+"F0.imprint","IMPRINT",FACE,{"disambiguationData":[TD([[makeQuery(id+"F0.imprint","IMPRINT",EDGE,{"derivedFrom":sQuery(id+"F0.wireOp",EDGE,"cwcGDYbz-mQkW-6XEh-srIc-m3WVtkQsgg1y")}),1.0]])]});
            var Q15;
            Q15=makeQuery(id+"F0.imprint","IMPRINT",FACE,{"disambiguationData":[TD([[makeQuery(id+"F0.imprint","IMPRINT",EDGE,{"derivedFrom":sQuery(id+"F0.wireOp",EDGE,"E5")}),1.0]])]});
            var Q16;
            {var subQ0=sQuery(id+"F0.wireOp",EDGE,"E49");Q16=makeQuery(id+"F0.imprint","IMPRINT",FACE,{"disambiguationData":[TD([[makeQuery(id+"F0.imprint","IMPRINT",EDGE,{"derivedFrom":subQ0}),-1.0]])]});}
            var Q17;
            Q17=makeQuery(id+"F0.imprint","IMPRINT",FACE,{"disambiguationData":[TD([[makeQuery(id+"F0.imprint","IMPRINT",EDGE,{"derivedFrom":sQuery(id+"F0.wireOp",EDGE,"E61")}),-1.0]])]});
            var Q18;
            Q18=makeQuery(id+"F0.imprint","IMPRINT",FACE,{"disambiguationData":[TD([[makeQuery(id+"F0.imprint","IMPRINT",EDGE,{"derivedFrom":sQuery(id+"F0.wireOp",EDGE,"E42")}),1.0]])]});
            var Q19;
            {var subQ3=sQuery(id+"F0.wireOp",EDGE,"E102");Q19=makeQuery(id+"F0.imprint","IMPRINT",FACE,{"disambiguationData":[TD([[makeQuery(id+"F0.imprint","IMPRINT",EDGE,{"derivedFrom":subQ3}),-1.0]])]});}
            var Q20;
            {var subQ0=sQuery(id+"F0.wireOp",EDGE,"E103");Q20=makeQuery(id+"F0.imprint","IMPRINT",FACE,{"disambiguationData":[TD([[makeQuery(id+"F0.imprint","IMPRINT",EDGE,{"derivedFrom":subQ0}),1.0]])]});}
            var Q21;
            {var subQ0=sQuery(id+"F0.wireOp",EDGE,"E105");Q21=makeQuery(id+"F0.imprint","IMPRINT",FACE,{"disambiguationData":[TD([[makeQuery(id+"F0.imprint","IMPRINT",EDGE,{"derivedFrom":subQ0}),1.0]])]});}
            var Q22;
            {var subQ0=sQuery(id+"F0.wireOp",EDGE,"E107");Q22=makeQuery(id+"F0.imprint","IMPRINT",FACE,{"disambiguationData":[TD([[makeQuery(id+"F0.imprint","IMPRINT",EDGE,{"derivedFrom":subQ0}),1.0]])]});}
            var Q23;
            {var subQ0=sQuery(id+"F0.wireOp",EDGE,"E109");Q23=makeQuery(id+"F0.imprint","IMPRINT",FACE,{"disambiguationData":[TD([[makeQuery(id+"F0.imprint","IMPRINT",EDGE,{"derivedFrom":subQ0}),1.0]])]});}
            var Q24;
            {var subQ0=sQuery(id+"F0.wireOp",EDGE,"E111");Q24=makeQuery(id+"F0.imprint","IMPRINT",FACE,{"disambiguationData":[TD([[makeQuery(id+"F0.imprint","IMPRINT",EDGE,{"derivedFrom":subQ0}),1.0]])]});}
            var Q25;
            {var subQ3=sQuery(id+"F0.wireOp",EDGE,"E113");Q25=makeQuery(id+"F0.imprint","IMPRINT",FACE,{"disambiguationData":[TD([[makeQuery(id+"F0.imprint","IMPRINT",EDGE,{"derivedFrom":subQ3}),-1.0]])]});}
            extrude(context, id + "F3", {"entities" : qUnion([Q0, Q1, Q2, Q3, Q4, Q5, Q6, Q7, Q8, Q9, Q10, Q11, Q12, Q13, Q14, Q15, Q16, Q17, Q18, Q19, Q20, Q21, Q22, Q23, Q24, Q25]), "depth" : 5.08 * mm, "offsetDistance" : 25.4 * mm});
        }
        {
            var Q0;
            {var subQ1=sQuery(id+"F1.wireOp",EDGE,"TzFiKtob-7T3S-KFg3-ROMa-pL2IaNzAbFjv");Q0=makeQuery(id+"F1.imprint","IMPRINT",FACE,{"disambiguationData":[TD([[makeQuery(id+"F1.imprint","IMPRINT",EDGE,{"derivedFrom":subQ1}),1.0]])]});}
            var Q1;
            {var subQ1=sQuery(id+"F1.wireOp",EDGE,"D8PxPf0Z-WsJ6-4OsX-Z8Az-UOjTWyzayGx0");Q1=makeQuery(id+"F1.imprint","IMPRINT",FACE,{"disambiguationData":[TD([[makeQuery(id+"F1.imprint","IMPRINT",EDGE,{"derivedFrom":subQ1}),1.0]])]});}
            var Q2;
            {var subQ4=sQuery(id+"F1.wireOp",EDGE,"E116");Q2=makeQuery(id+"F1.imprint","IMPRINT",FACE,{"disambiguationData":[TD([[makeQuery(id+"F1.imprint","IMPRINT",EDGE,{"derivedFrom":subQ4}),-1.0]])]});}
            var Q3;
            {var subQ3=sQuery(id+"F1.wireOp",EDGE,"E117");Q3=makeQuery(id+"F1.imprint","IMPRINT",FACE,{"disambiguationData":[TD([[makeQuery(id+"F1.imprint","IMPRINT",EDGE,{"derivedFrom":subQ3}),-1.0]])]});}
            var Q4;
            {var subQ1=sQuery(id+"F1.wireOp",EDGE,"E120");Q4=makeQuery(id+"F1.imprint","IMPRINT",FACE,{"disambiguationData":[TD([[makeQuery(id+"F1.imprint","IMPRINT",EDGE,{"derivedFrom":subQ1}),1.0]])]});}
            var Q5;
            {var subQ3=sQuery(id+"F1.wireOp",EDGE,"E122");Q5=makeQuery(id+"F1.imprint","IMPRINT",FACE,{"disambiguationData":[TD([[makeQuery(id+"F1.imprint","IMPRINT",EDGE,{"derivedFrom":subQ3}),-1.0]])]});}
            var Q6;
            {var subQ1=sQuery(id+"F1.wireOp",EDGE,"E124");Q6=makeQuery(id+"F1.imprint","IMPRINT",FACE,{"disambiguationData":[TD([[makeQuery(id+"F1.imprint","IMPRINT",EDGE,{"derivedFrom":subQ1}),1.0]])]});}
            var Q7;
            {var subQ3=sQuery(id+"F1.wireOp",EDGE,"E125");Q7=makeQuery(id+"F1.imprint","IMPRINT",FACE,{"disambiguationData":[TD([[makeQuery(id+"F1.imprint","IMPRINT",EDGE,{"derivedFrom":subQ3}),-1.0]])]});}
            var Q8;
            {var subQ7=sQuery(id+"F1.wireOp",EDGE,"E128");Q8=makeQuery(id+"F1.imprint","IMPRINT",FACE,{"disambiguationData":[TD([[makeQuery(id+"F1.imprint","IMPRINT",EDGE,{"derivedFrom":subQ7}),-1.0]])]});}
            var Q9;
            {var subQ4=sQuery(id+"F1.wireOp",EDGE,"E129");Q9=makeQuery(id+"F1.imprint","IMPRINT",FACE,{"disambiguationData":[TD([[makeQuery(id+"F1.imprint","IMPRINT",EDGE,{"derivedFrom":subQ4}),1.0]])]});}
            var Q10;
            {var subQ4=sQuery(id+"F1.wireOp",EDGE,"E132");Q10=makeQuery(id+"F1.imprint","IMPRINT",FACE,{"disambiguationData":[TD([[makeQuery(id+"F1.imprint","IMPRINT",EDGE,{"derivedFrom":subQ4}),1.0]])]});}
            var Q11;
            {var subQ3=sQuery(id+"F1.wireOp",EDGE,"E133");Q11=makeQuery(id+"F1.imprint","IMPRINT",FACE,{"disambiguationData":[TD([[makeQuery(id+"F1.imprint","IMPRINT",EDGE,{"derivedFrom":subQ3}),1.0]])]});}
            var Q12;
            Q12=makeQuery(id+"F1.imprint","IMPRINT",FACE,{"disambiguationData":[TD([[makeQuery(id+"F1.imprint","IMPRINT",EDGE,{"derivedFrom":sQuery(id+"F1.wireOp",EDGE,"E173")}),1.0]])]});
            var Q13;
            Q13=makeQuery(id+"F1.imprint","IMPRINT",FACE,{"disambiguationData":[TD([[makeQuery(id+"F1.imprint","IMPRINT",EDGE,{"derivedFrom":sQuery(id+"F1.wireOp",EDGE,"b4WOXvqN-aaSw-bhnN-ur1f-cWbwp9thIOQV")}),1.0]])]});
            var Q14;
            Q14=makeQuery(id+"F1.imprint","IMPRINT",FACE,{"disambiguationData":[TD([[makeQuery(id+"F1.imprint","IMPRINT",EDGE,{"derivedFrom":sQuery(id+"F1.wireOp",EDGE,"E165")}),-1.0]])]});
            var Q15;
            Q15=makeQuery(id+"F1.imprint","IMPRINT",FACE,{"disambiguationData":[TD([[makeQuery(id+"F1.imprint","IMPRINT",EDGE,{"derivedFrom":sQuery(id+"F1.wireOp",EDGE,"E163")}),1.0]])]});
            var Q16;
            Q16=makeQuery(id+"F1.imprint","IMPRINT",FACE,{"disambiguationData":[TD([[makeQuery(id+"F1.imprint","IMPRINT",EDGE,{"derivedFrom":sQuery(id+"F1.wireOp",EDGE,"E185")}),-1.0]])]});
            extrude(context, id + "F4", {"entities" : qUnion([Q0, Q1, Q2, Q3, Q4, Q5, Q6, Q7, Q8, Q9, Q10, Q11, Q12, Q13, Q14, Q15, Q16]), "depth" : 7.62 * mm, "offsetDistance" : 25.4 * mm});
        }
    });
